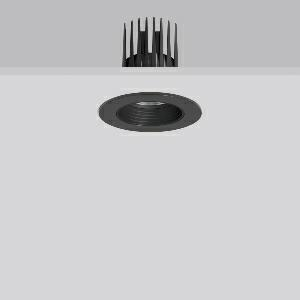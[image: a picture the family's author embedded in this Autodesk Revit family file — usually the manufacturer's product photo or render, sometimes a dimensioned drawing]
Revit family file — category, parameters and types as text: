
# Revit family: heledon_mini_e_901747_003_1_02f5
name_source: partatom
category: Lighting Fixtures
units: mm (PartAtom-declared; Revit-internal decimal feet)

## family parameters
Cut with Voids When Loaded = No
Host = Face
Light Source = No
Part Type = Normal
Room Calculation Point = No
Round Connector Dimension = Use Diameter
Shared = No

## types (1)
- HELEDON mini E (1 x LED Modul 940, 2050 lm, 4000)
    Apparent Load = 20 VA
    Approval mark = CE
    CIE Flux Codes = 95 100 100 100 100
    Color Rendering = 92
    Color Temperature = 4000
    Default Elevation = 1800 mm
    Description = Series: HELEDON mini
Round recessed downlight. Housing: die-cast aluminium, powder-coated. Black plastic ring and recessed LED to prevent glare from the side. Optical assembly with lens made of plastic (polycarbonate) for the best homogeneous light distribution - can be changed without tools. Best colour rendering index Ra>90. Suitable for Recessed ceiling mounting. Installation without tools thanks to spring fastening system. Including separate LED converter with connecting cable 600 mm.High quality converter without flickering and stroboscopic effect. Through-wiring box (5 pole) available as accessory. The following accessories can be mounted without use of tools: interchangeable lenses, decorative glasses, honeycomb louvre, clear and frosted diffusers, white interchangeable plastic ring. 
Colour: deep black, matt (RAL 9005)
Diameter: 124 mm
Height: 3 mm
Cut-out diameter: 114 mm
Recess height: 170 mm
Luminaire: recess height: 120 mm
Lamp: LED
Socket: without socket
Colour temperature: 4000K
Colour rendering index (CRI): 92
System power: 20 W
Rated luminous flux: 2050 lm
Luminous efficiency: 103 lm/W
Control gear: Regulated power supply
Protection class: II
Type of protection: IP 20
    Height = 0 mm  [stored 0 ft]
    Lamp = 1 x LED Modul 940
    Lamp Light Flux = 2050 lm
    Lamp count = 1
    Length = 124 mm
    Lifetime = 50000 h
    Luminous efficacy = 103 lm/W
    Manufacturer = RZB
    ModVariant = No
    Model = 901747.003.1
    Mounting Place = Ceiling
    Mounting Type = Recessed
    Number of Poles = 1
    OnlyDefault = Yes
    Power Factor = 1
    Product Name = HELEDON mini E
    Product group = Recessed downlights
    ProductGroupID = 402
    Protection Class = Protection class II
    Protection Degree = IP 20
    RLX_Detail_Level = 1
    RLX_Emergency_Light_Flux = 0 lm
    RLX_Emergency_Type = 0
    RLX_Emergency_Type_DB = No
    RlxData = <blob elided: 134081 chars, md5=fb08c61f>
    Socket = socket
    Standby Power = 0 W
    System Light Flux = 2050 lm
    System Power = 20 W
    Type Comments = Product without accessories
    Type Image = 901656.003.jpg
    URL = http://relux.com
    VarID = ---
    Voltage = 230 V
    Voltage Range = 220-240 V
    Weight = 0.00 kg
    Width = 0 mm  [stored 0 ft]

note: [stored X ft] marks values corroborated as IEEE doubles in the binary element streams (Revit-internal decimal feet)

## geometry (parser evidence)
native form markers: Blend x4, Sweep x11
no freeform markers — native parametric forms only
